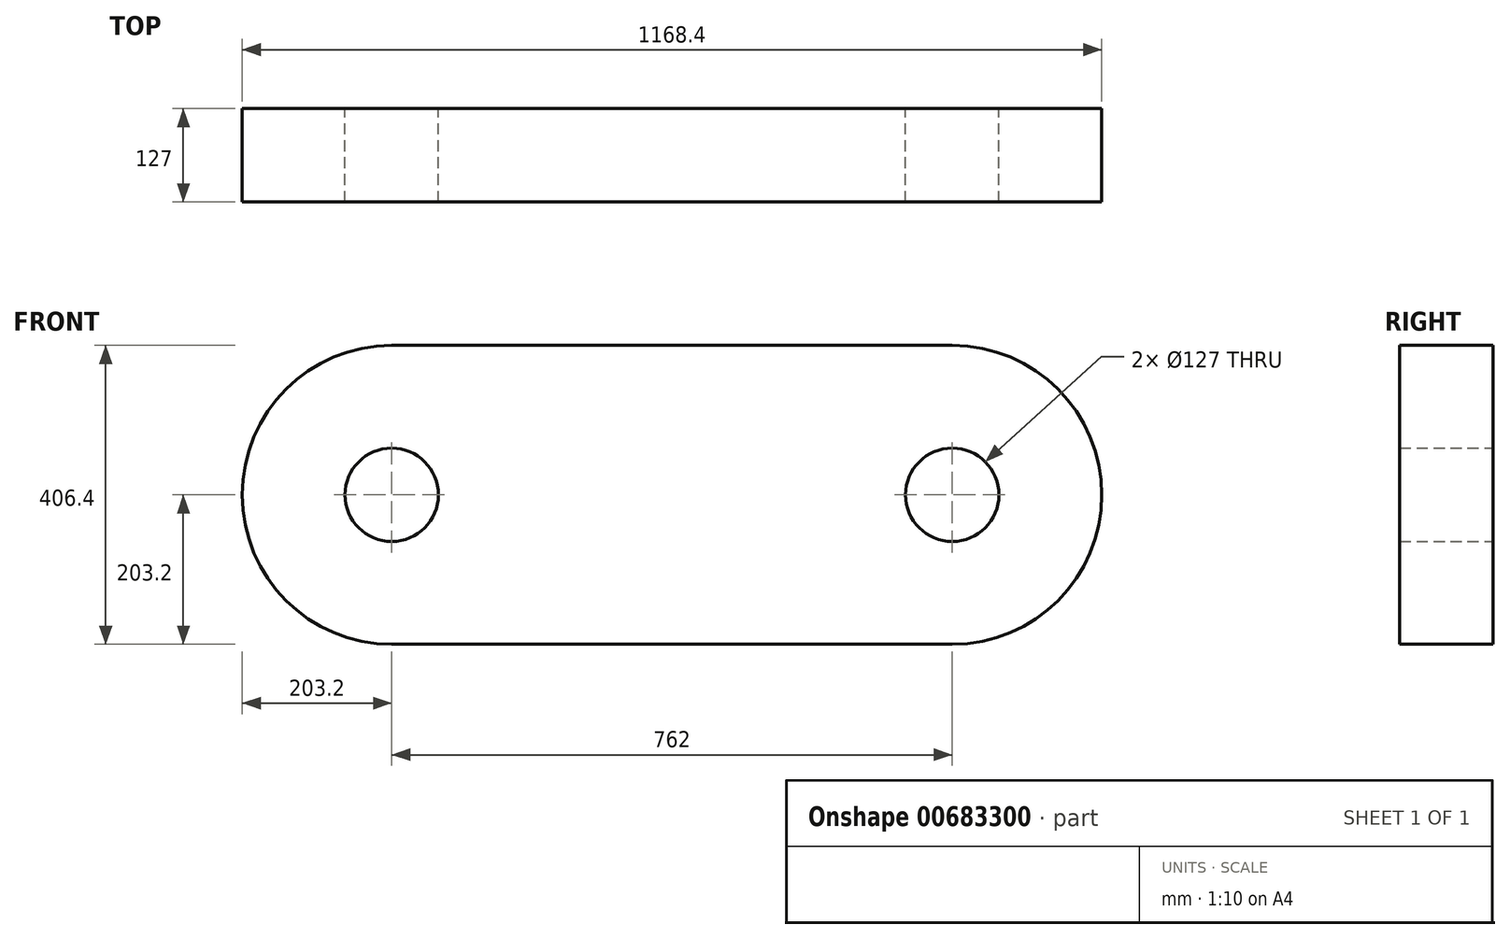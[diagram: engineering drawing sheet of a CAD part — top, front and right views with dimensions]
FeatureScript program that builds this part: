
annotation { "Feature Type Name" : "Feature", "Feature Type Description" : "" }
export const myFeature = defineFeature(function(context is Context, id is Id, definition is map)
    precondition{}
    {
        {
            var Q0;
            Q0=qCreatedBy(makeId("Front.planeOp"),FACE);
            var sketch = newSketch(context, id + "F0", { "sketchPlane" : qUnion([Q0])});
            skLineSegment(sketch, "E0.bottom", {"start": v(-381, 203.2) * mm, "end": v(381, 203.2) * mm});
            skLineSegment(sketch, "E0.top", {"start": v(-381, -203.2) * mm, "end": v(381, -203.2) * mm});
            skArc(sketch, "E1", {"start": v(-381, 203.2) * mm, "mid": v(-584.2, 0) * mm, "end": v(-381, -203.2) * mm});
            skArc(sketch, "E2", {"start": v(381, -203.2) * mm, "mid": v(584.2, 0) * mm, "end": v(381, 203.2) * mm});
            skCircle(sketch, "E3", {"center": v(-381, 0) * mm, "radius": 63.5 * mm});
            skCircle(sketch, "E4", {"center": v(381, 0) * mm, "radius": 63.5 * mm});
            skSolve(sketch);
        }
        {
            var Q0;
            Q0=qSketchRegion(id+"F0",true);
            extrude(context, id + "F1", {"entities" : qUnion([Q0]), "depth" : 127 * mm, "offsetDistance" : 25.4 * mm});
        }
    });
